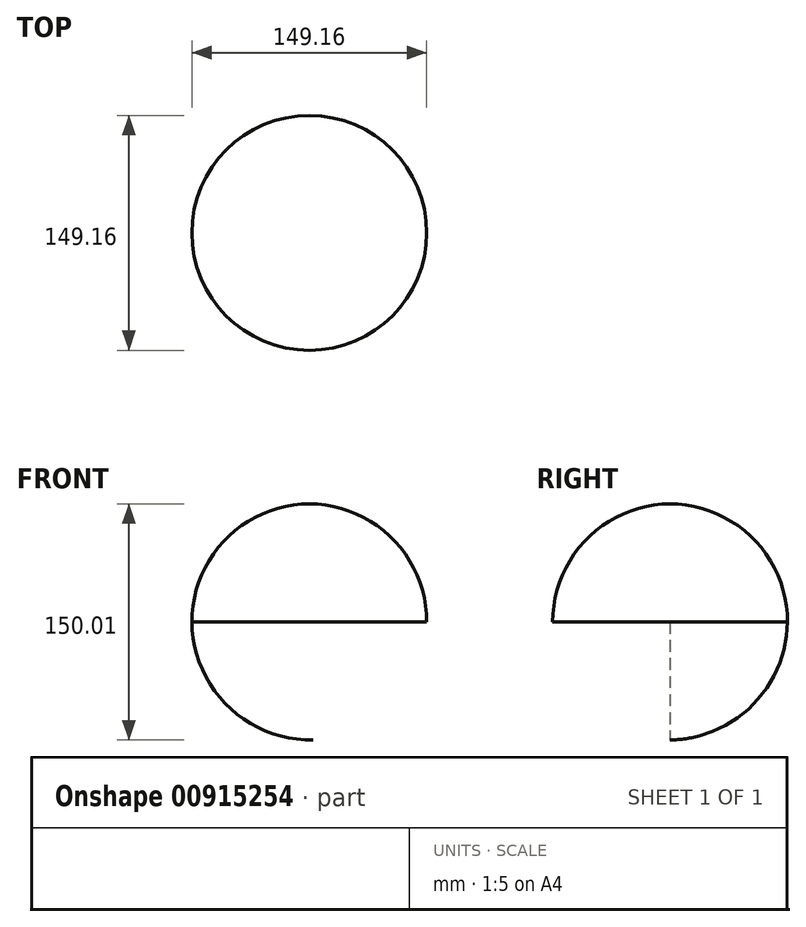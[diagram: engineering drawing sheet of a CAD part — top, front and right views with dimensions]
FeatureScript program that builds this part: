
annotation { "Feature Type Name" : "Feature", "Feature Type Description" : "" }
export const myFeature = defineFeature(function(context is Context, id is Id, definition is map)
    precondition{}
    {
        {
            var Q0;
            Q0=qCreatedBy(makeId("Front.planeOp"),FACE);
            var sketch = newSketch(context, id + "F0", { "sketchPlane" : qUnion([Q0])});
            skArc(sketch, "E0", {"start": v(0, 75) * mm, "mid": v(-52.75, 52.87) * mm, "end": v(-74.58, 0) * mm});
            skArc(sketch, "E1", {"start": v(-74.58, 0) * mm, "mid": v(-52.54, -52.67) * mm, "end": v(0, -75) * mm});
            skLineSegment(sketch, "E2", {"start": v(0, 75) * mm, "end": v(0, -75) * mm});
            skSolve(sketch);
        }
        {
            var Q0;
            Q0=makeQuery(id+"F0.imprint","IMPRINT",FACE,{"disambiguationData":[TD([[makeQuery(id+"F0.imprint","IMPRINT",EDGE,{"derivedFrom":sQuery(id+"F0.wireOp",EDGE,"E0")}),1.0]])]});
            var Q1;
            Q1=sQuery(id+"F0.wireOp",EDGE,"E2");
            revolve(context, id + "F1", {"surfaceOperationType" : NewSurfaceOperationType.NEW, "entities" : qUnion([Q0]), "axis" : qUnion([Q1]), "revolveType" : RevolveType.FULL});
        }
    });
